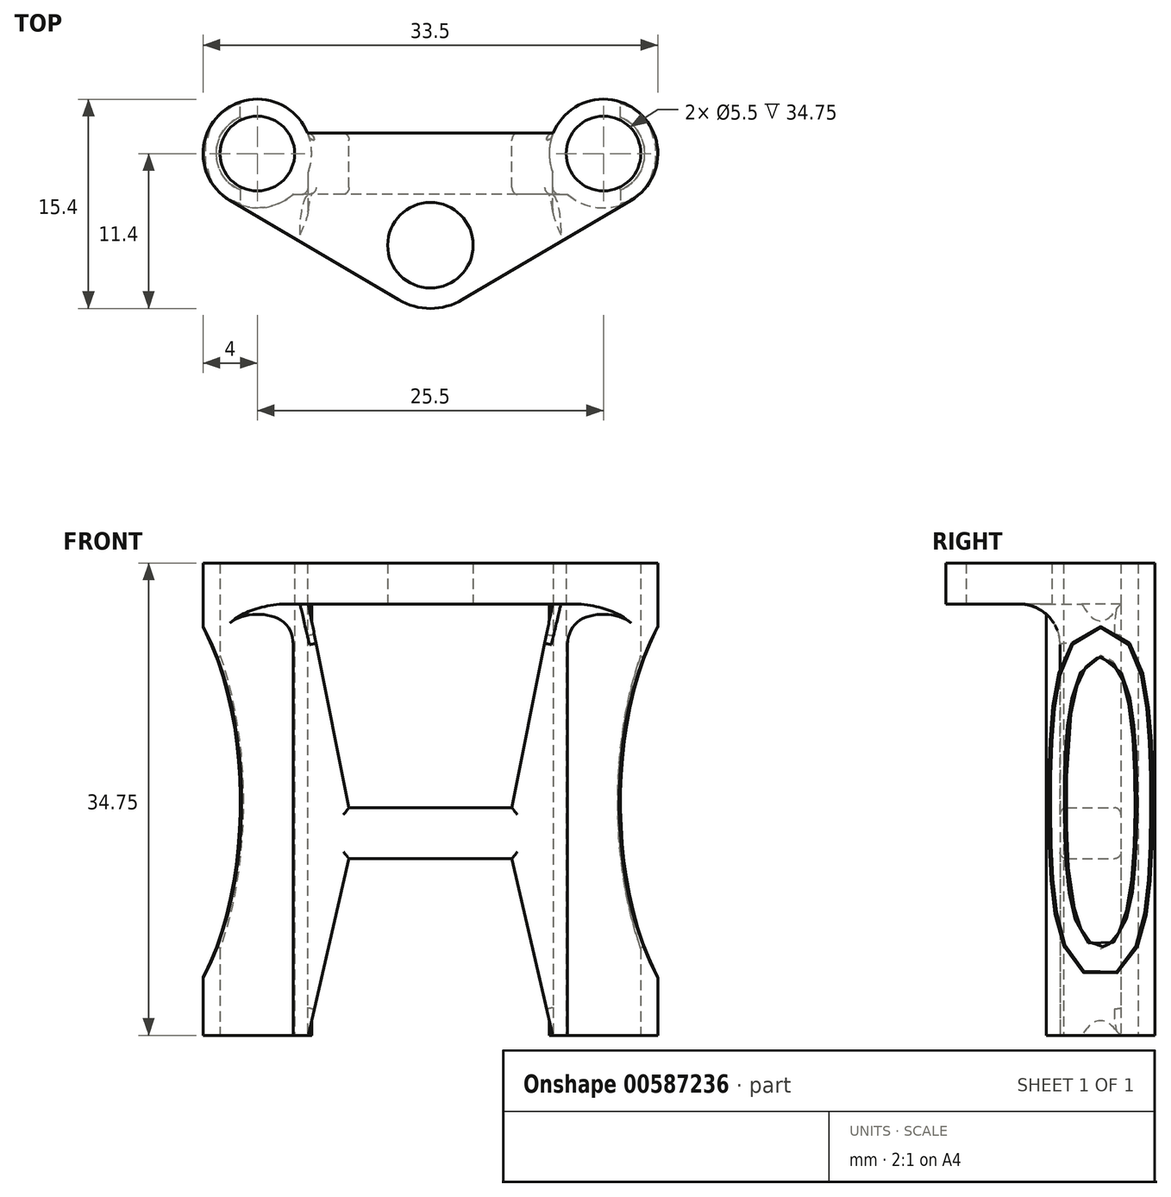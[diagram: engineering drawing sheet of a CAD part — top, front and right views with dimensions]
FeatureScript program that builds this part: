
annotation { "Feature Type Name" : "Feature", "Feature Type Description" : "" }
export const myFeature = defineFeature(function(context is Context, id is Id, definition is map)
    precondition{}
    {
        {
            var Q0;
            Q0=qCreatedBy(makeId("Top.planeOp"),FACE);
            var sketch = newSketch(context, id + "F0", { "sketchPlane" : qUnion([Q0])});
            skCircle(sketch, "E0", {"center": v(0, -6.75) * mm, "radius": 4.65 * mm});
            skCircle(sketch, "E1", {"center": v(0, -6.75) * mm, "radius": 3.15 * mm});
            skCircle(sketch, "E2", {"center": v(-12.75, 0) * mm, "radius": 4 * mm});
            skCircle(sketch, "E3", {"center": v(-12.75, 0) * mm, "radius": 2.75 * mm});
            skCircle(sketch, "E4", {"center": v(12.75, 0) * mm, "radius": 4 * mm});
            skCircle(sketch, "E5", {"center": v(12.75, 0) * mm, "radius": 2.75 * mm});
            skLineSegment(sketch, "E6", {"start": v(0, 0) * mm, "end": v(0, -6.75) * mm});
            skLineSegment(sketch, "E7", {"start": v(-14.78, -3.45) * mm, "end": v(-2.36, -10.76) * mm});
            skLineSegment(sketch, "E8", {"start": v(2.36, -10.76) * mm, "end": v(14.78, -3.45) * mm});
            skLineSegment(sketch, "E9", {"start": v(-9.04, 1.5) * mm, "end": v(9.04, 1.5) * mm});
            skLineSegment(sketch, "E10", {"start": v(-12.75, 0) * mm, "end": v(0, 0) * mm});
            skLineSegment(sketch, "E11", {"start": v(0, 0) * mm, "end": v(12.75, 0) * mm});
            skLineSegment(sketch, "E12", {"start": v(-9.04, -1.5) * mm, "end": v(9.04, -1.5) * mm});
            skSolve(sketch);
        }
        {
            var Q0;
            Q0=makeQuery(id+"F0.imprint","IMPRINT",FACE,{"disambiguationData":[TD([[makeQuery(id+"F0.imprint","IMPRINT",EDGE,{"derivedFrom":sQuery(id+"F0.wireOp",EDGE,"E3")}),-1.0]])]});
            var Q1;
            {var subQ0=sQuery(id+"F0.wireOp",EDGE,"E9");Q1=makeQuery(id+"F0.imprint","IMPRINT",FACE,{"disambiguationData":[TD([[makeQuery(id+"F0.imprint","IMPRINT",EDGE,{"derivedFrom":subQ0}),-1.0]])]});}
            var Q2;
            {var subQ0=sQuery(id+"F0.wireOp",EDGE,"E12");var subQ1=sQuery(id+"F0.wireOp",EDGE,"E2");var subQ2=makeQuery(id+"F0.imprint","INTERSECT",VERTEX,{"derivedFrom":[subQ1,subQ0]});Q2=makeQuery(id+"F0.imprint","IMPRINT",FACE,{"disambiguationData":[TD([[makeQuery(id+"F0.imprint","IMPRINT",EDGE,{"disambiguationData":[TD([[subQ2,-1.0]])],"derivedFrom":subQ1}),-1.0]])]});}
            var Q3;
            Q3=makeQuery(id+"F0.imprint","IMPRINT",FACE,{"disambiguationData":[TD([[makeQuery(id+"F0.imprint","IMPRINT",EDGE,{"derivedFrom":sQuery(id+"F0.wireOp",EDGE,"E5")}),-1.0]])]});
            var Q4;
            {var subQ0=sQuery(id+"F0.wireOp",EDGE,"E12");var subQ1=sQuery(id+"F0.wireOp",EDGE,"E4");var subQ2=makeQuery(id+"F0.imprint","INTERSECT",VERTEX,{"derivedFrom":[subQ1,subQ0]});Q4=makeQuery(id+"F0.imprint","IMPRINT",FACE,{"disambiguationData":[TD([[makeQuery(id+"F0.imprint","IMPRINT",EDGE,{"disambiguationData":[TD([[subQ2,1.0]])],"derivedFrom":subQ1}),-1.0]])]});}
            var Q5;
            {var subQ0=sQuery(id+"F0.wireOp",EDGE,"E7");Q5=makeQuery(id+"F0.imprint","IMPRINT",FACE,{"disambiguationData":[TD([[makeQuery(id+"F0.imprint","IMPRINT",EDGE,{"derivedFrom":subQ0}),1.0]])]});}
            var Q6;
            {var subQ5=sQuery(id+"F0.wireOp",EDGE,"E8");Q6=makeQuery(id+"F0.imprint","IMPRINT",FACE,{"disambiguationData":[TD([[makeQuery(id+"F0.imprint","IMPRINT",EDGE,{"derivedFrom":subQ5}),1.0]])]});}
            var Q7;
            Q7=makeQuery(id+"F0.imprint","IMPRINT",FACE,{"disambiguationData":[TD([[makeQuery(id+"F0.imprint","IMPRINT",EDGE,{"derivedFrom":sQuery(id+"F0.wireOp",EDGE,"E1")}),-1.0]])]});
            extrude(context, id + "F1", {"entities" : qUnion([Q0, Q1, Q2, Q3, Q4, Q5, Q6, Q7]), "depth" : 34.75 * mm, "offsetDistance" : 25 * mm});
        }
        {
            var Q0;
            Q0=qCreatedBy(makeId("Front.planeOp"),FACE);
            var sketch = newSketch(context, id + "F2", { "sketchPlane" : qUnion([Q0])});
            skLineSegment(sketch, "E13", {"start": v(0, 0) * mm, "end": v(-9, 0) * mm});
            skLineSegment(sketch, "E14", {"start": v(-9, 0) * mm, "end": v(-6, 13) * mm});
            skLineSegment(sketch, "E15", {"start": v(-6, 13) * mm, "end": v(6, 13) * mm});
            skLineSegment(sketch, "E16", {"start": v(6, 13) * mm, "end": v(9, 0) * mm});
            skLineSegment(sketch, "E17", {"start": v(9, 0) * mm, "end": v(0, 0) * mm});
            skLineSegment(sketch, "E18", {"start": v(0, 31.75) * mm, "end": v(-9, 31.75) * mm});
            skLineSegment(sketch, "E19", {"start": v(-9, 31.75) * mm, "end": v(-6, 16.75) * mm});
            skLineSegment(sketch, "E20", {"start": v(-6, 16.75) * mm, "end": v(6, 16.75) * mm});
            skLineSegment(sketch, "E21", {"start": v(6, 16.75) * mm, "end": v(9, 31.75) * mm});
            skLineSegment(sketch, "E22", {"start": v(9, 31.75) * mm, "end": v(0, 31.75) * mm});
            skSolve(sketch);
        }
        {
            var Q0;
            Q0 = qSketchRegion(id + "F2", true);
            extrude(context, id + "F3", {"entities" : qUnion([Q0]), "operationType" : NewBodyOperationType.REMOVE, "endBound" : BoundingType.SYMMETRIC, "depth" : 25 * mm, "offsetDistance" : 25 * mm});
        }
        {
            var Q0;
            Q0=qCreatedBy(makeId("Right.planeOp"),FACE);
            var sketch = newSketch(context, id + "F4", { "sketchPlane" : qUnion([Q0])});
            skLineSegment(sketch, "E23", {"start": v(-3, 0) * mm, "end": v(-3, 28.75) * mm});
            skLineSegment(sketch, "E24", {"start": v(-6, 31.75) * mm, "end": v(-18, 31.75) * mm});
            skLineSegment(sketch, "E25", {"start": v(-18, 31.75) * mm, "end": v(-18, 0) * mm});
            skLineSegment(sketch, "E26", {"start": v(-18, 0) * mm, "end": v(-3, 0) * mm});
            skPoint(sketch, "E27.visualSharp", {"position": v(-3, 31.75) * mm});
            skArc(sketch, "E27.filletArc", {"start": v(-3, 28.75) * mm, "mid": v(-3.88, 30.87) * mm, "end": v(-6, 31.75) * mm});
            skSolve(sketch);
        }
        {
            var Q0;
            Q0 = qSketchRegion(id + "F4", true);
            extrude(context, id + "F5", {"entities" : qUnion([Q0]), "operationType" : NewBodyOperationType.REMOVE, "endBound" : BoundingType.SYMMETRIC, "oppositeDirection" : true, "depth" : 35 * mm, "offsetDistance" : 25 * mm});
        }
        {
            var Q0;
            Q0=makeQuery(id+"F5.boolean.opBoolean","INTERSECT",EDGE,{"derivedFrom":[makeQuery(id+"F3.boolean.opBoolean","COPY",FACE,{"derivedFrom":makeQuery(id+"F3.opExtrude","SWEPT_FACE",FACE,{"disambiguationData":[OSD([sQuery(id+"F2.wireOp",EDGE,"E19")])]})}),makeQuery(id+"F5.opExtrude","SWEPT_FACE",FACE,{"disambiguationData":[OSD([sQuery(id+"F4.wireOp",EDGE,"E23")])]})]});
            var Q1;
            Q1=makeQuery(id+"F5.boolean.opBoolean","INTERSECT",EDGE,{"derivedFrom":[makeQuery(id+"F3.boolean.opBoolean","COPY",FACE,{"derivedFrom":makeQuery(id+"F3.opExtrude","SWEPT_FACE",FACE,{"disambiguationData":[OSD([sQuery(id+"F2.wireOp",EDGE,"E20")])]})}),makeQuery(id+"F5.opExtrude","SWEPT_FACE",FACE,{"disambiguationData":[OSD([sQuery(id+"F4.wireOp",EDGE,"E23")])]})]});
            var Q2;
            Q2=makeQuery(id+"F5.boolean.opBoolean","INTERSECT",EDGE,{"derivedFrom":[makeQuery(id+"F3.boolean.opBoolean","COPY",FACE,{"derivedFrom":makeQuery(id+"F3.opExtrude","SWEPT_FACE",FACE,{"disambiguationData":[OSD([sQuery(id+"F2.wireOp",EDGE,"E21")])]})}),makeQuery(id+"F5.opExtrude","SWEPT_FACE",FACE,{"disambiguationData":[OSD([sQuery(id+"F4.wireOp",EDGE,"E23")])]})]});
            var Q3;
            Q3=makeQuery(id+"F5.boolean.opBoolean","INTERSECT",EDGE,{"derivedFrom":[makeQuery(id+"F3.boolean.opBoolean","COPY",FACE,{"derivedFrom":makeQuery(id+"F3.opExtrude","SWEPT_FACE",FACE,{"disambiguationData":[OSD([sQuery(id+"F2.wireOp",EDGE,"E16")])]})}),makeQuery(id+"F5.opExtrude","SWEPT_FACE",FACE,{"disambiguationData":[OSD([sQuery(id+"F4.wireOp",EDGE,"E23")])]})]});
            var Q4;
            Q4=makeQuery(id+"F5.boolean.opBoolean","INTERSECT",EDGE,{"derivedFrom":[makeQuery(id+"F3.boolean.opBoolean","COPY",FACE,{"derivedFrom":makeQuery(id+"F3.opExtrude","SWEPT_FACE",FACE,{"disambiguationData":[OSD([sQuery(id+"F2.wireOp",EDGE,"E15")])]})}),makeQuery(id+"F5.opExtrude","SWEPT_FACE",FACE,{"disambiguationData":[OSD([sQuery(id+"F4.wireOp",EDGE,"E23")])]})]});
            var Q5;
            Q5=makeQuery(id+"F5.boolean.opBoolean","INTERSECT",EDGE,{"derivedFrom":[makeQuery(id+"F3.boolean.opBoolean","COPY",FACE,{"derivedFrom":makeQuery(id+"F3.opExtrude","SWEPT_FACE",FACE,{"disambiguationData":[OSD([sQuery(id+"F2.wireOp",EDGE,"E14")])]})}),makeQuery(id+"F5.opExtrude","SWEPT_FACE",FACE,{"disambiguationData":[OSD([sQuery(id+"F4.wireOp",EDGE,"E23")])]})]});
            var Q6;
            Q6=makeQuery(id+"F3.boolean.opBoolean","INTERSECT",EDGE,{"derivedFrom":[makeQuery(id+"F1.opExtrude","SWEPT_FACE",FACE,{"disambiguationData":[OSD([sQuery(id+"F0.wireOp",EDGE,"E9")])]}),makeQuery(id+"F3.opExtrude","SWEPT_FACE",FACE,{"disambiguationData":[OSD([sQuery(id+"F2.wireOp",EDGE,"E16")])]})]});
            var Q7;
            Q7=makeQuery(id+"F3.boolean.opBoolean","INTERSECT",EDGE,{"derivedFrom":[makeQuery(id+"F1.opExtrude","SWEPT_FACE",FACE,{"disambiguationData":[OSD([sQuery(id+"F0.wireOp",EDGE,"E9")])]}),makeQuery(id+"F3.opExtrude","SWEPT_FACE",FACE,{"disambiguationData":[OSD([sQuery(id+"F2.wireOp",EDGE,"E15")])]})]});
            var Q8;
            Q8=makeQuery(id+"F3.boolean.opBoolean","INTERSECT",EDGE,{"derivedFrom":[makeQuery(id+"F1.opExtrude","SWEPT_FACE",FACE,{"disambiguationData":[OSD([sQuery(id+"F0.wireOp",EDGE,"E9")])]}),makeQuery(id+"F3.opExtrude","SWEPT_FACE",FACE,{"disambiguationData":[OSD([sQuery(id+"F2.wireOp",EDGE,"E14")])]})]});
            var Q9;
            Q9=makeQuery(id+"F3.boolean.opBoolean","INTERSECT",EDGE,{"derivedFrom":[makeQuery(id+"F1.opExtrude","SWEPT_FACE",FACE,{"disambiguationData":[OSD([sQuery(id+"F0.wireOp",EDGE,"E9")])]}),makeQuery(id+"F3.opExtrude","SWEPT_FACE",FACE,{"disambiguationData":[OSD([sQuery(id+"F2.wireOp",EDGE,"E21")])]})]});
            var Q10;
            Q10=makeQuery(id+"F3.boolean.opBoolean","INTERSECT",EDGE,{"derivedFrom":[makeQuery(id+"F1.opExtrude","SWEPT_FACE",FACE,{"disambiguationData":[OSD([sQuery(id+"F0.wireOp",EDGE,"E9")])]}),makeQuery(id+"F3.opExtrude","SWEPT_FACE",FACE,{"disambiguationData":[OSD([sQuery(id+"F2.wireOp",EDGE,"E20")])]})]});
            var Q11;
            Q11=makeQuery(id+"F3.boolean.opBoolean","INTERSECT",EDGE,{"derivedFrom":[makeQuery(id+"F1.opExtrude","SWEPT_FACE",FACE,{"disambiguationData":[OSD([sQuery(id+"F0.wireOp",EDGE,"E9")])]}),makeQuery(id+"F3.opExtrude","SWEPT_FACE",FACE,{"disambiguationData":[OSD([sQuery(id+"F2.wireOp",EDGE,"E19")])]})]});
            fillet(context, id + "F6", {"entities" : qUnion([Q0, Q1, Q2, Q3, Q4, Q5, Q6, Q7, Q8, Q9, Q10, Q11]), "radius" : 0.5 * mm, "tangentPropagation" : true, "allowEdgeOverflow" : false});
        }
        {
            var Q0;
            Q0=qCreatedBy(makeId("Top.planeOp"),FACE);
            var sketch = newSketch(context, id + "F7", { "sketchPlane" : qUnion([Q0])});
            skCircle(sketch, "E28", {"center": v(-12.75, 0) * mm, "radius": 4 * mm});
            skCircle(sketch, "E29", {"center": v(12.75, 0) * mm, "radius": 4 * mm});
            skCircle(sketch, "E30", {"center": v(-12.75, 0) * mm, "radius": 2.75 * mm});
            skCircle(sketch, "E31", {"center": v(12.75, 0) * mm, "radius": 2.75 * mm});
            skSolve(sketch);
        }
        {
            var Q0;
            Q0=makeQuery(id+"F7.imprint","IMPRINT",FACE,{"disambiguationData":[TD([[makeQuery(id+"F7.imprint","IMPRINT",EDGE,{"derivedFrom":sQuery(id+"F7.wireOp",EDGE,"E28")}),1.0]])]});
            var Q1;
            Q1=makeQuery(id+"F7.imprint","IMPRINT",FACE,{"disambiguationData":[TD([[makeQuery(id+"F7.imprint","IMPRINT",EDGE,{"derivedFrom":sQuery(id+"F7.wireOp",EDGE,"E29")}),1.0]])]});
            extrude(context, id + "F8", {"entities" : qUnion([Q0, Q1]), "operationType" : NewBodyOperationType.ADD, "depth" : 34.75 * mm, "offsetDistance" : 25 * mm});
        }
        {
            var Q0;
            Q0=qCreatedBy(makeId("Front.planeOp"),FACE);
            var sketch = newSketch(context, id + "F9", { "sketchPlane" : qUnion([Q0])});
            skEllipse(sketch, "E32", {"center": v(-22.5, 17.16) * mm, "majorRadius": 17.5 * mm, "minorRadius": 8.5 * mm, "majorAxis": v(0, -1)});
            skEllipse(sketch, "E33.MirrorC", {"center": v(22.5, 17.16) * mm, "majorRadius": 17.5 * mm, "minorRadius": 8.5 * mm, "majorAxis": v(0, -1)});
            skSolve(sketch);
        }
        {
            var Q0;
            Q0=makeQuery(id+"F9.imprint","IMPRINT",FACE,{"disambiguationData":[TD([[makeQuery(id+"F9.imprint","IMPRINT",EDGE,{"derivedFrom":sQuery(id+"F9.wireOp",EDGE,"E32")}),1.0]])]});
            var Q1;
            Q1=makeQuery(id+"F9.imprint","IMPRINT",FACE,{"disambiguationData":[TD([[makeQuery(id+"F9.imprint","IMPRINT",EDGE,{"derivedFrom":sQuery(id+"F9.wireOp",EDGE,"E33.MirrorC")}),1.0]])]});
            extrude(context, id + "F10", {"entities" : qUnion([Q0, Q1]), "operationType" : NewBodyOperationType.REMOVE, "endBound" : BoundingType.SYMMETRIC, "oppositeDirection" : true, "depth" : 25 * mm, "offsetDistance" : 25 * mm});
        }
        {
            var Q0;
            Q0=makeQuery(id+"F10.boolean.opBoolean","INTERSECT",EDGE,{"derivedFrom":[makeQuery(id+"F8.boolean.opBoolean","MERGE",FACE,{"derivedFrom":[makeQuery(id+"F1.opExtrude","SWEPT_FACE",FACE,{"disambiguationData":[OSD([sQuery(id+"F0.wireOp",EDGE,"E4")])]}),makeQuery(id+"F8.opExtrude","SWEPT_FACE",FACE,{"disambiguationData":[OSD([sQuery(id+"F7.wireOp",EDGE,"E29")])]})]}),makeQuery(id+"F10.opExtrude","SWEPT_FACE",FACE,{"disambiguationData":[OSD([sQuery(id+"F9.wireOp",EDGE,"E33.MirrorC")])]})]});
            var Q1;
            Q1=makeQuery(id+"F10.boolean.opBoolean","INTERSECT",EDGE,{"derivedFrom":[makeQuery(id+"F8.boolean.opBoolean","MERGE",FACE,{"derivedFrom":[makeQuery(id+"F1.opExtrude","SWEPT_FACE",FACE,{"disambiguationData":[OSD([sQuery(id+"F0.wireOp",EDGE,"E2")])]}),makeQuery(id+"F8.opExtrude","SWEPT_FACE",FACE,{"disambiguationData":[OSD([sQuery(id+"F7.wireOp",EDGE,"E28")])]})]}),makeQuery(id+"F10.opExtrude","SWEPT_FACE",FACE,{"disambiguationData":[OSD([sQuery(id+"F9.wireOp",EDGE,"E32")])]})]});
            var Q2;
            Q2=makeQuery(id+"F10.boolean.opBoolean","INTERSECT",EDGE,{"derivedFrom":[makeQuery(id+"F1.opExtrude","SWEPT_FACE",FACE,{"disambiguationData":[OSD([sQuery(id+"F0.wireOp",EDGE,"E3")])]}),makeQuery(id+"F10.opExtrude","SWEPT_FACE",FACE,{"disambiguationData":[OSD([sQuery(id+"F9.wireOp",EDGE,"E32")])]})]});
            var Q3;
            Q3=makeQuery(id+"F10.boolean.opBoolean","INTERSECT",EDGE,{"derivedFrom":[makeQuery(id+"F1.opExtrude","SWEPT_FACE",FACE,{"disambiguationData":[OSD([sQuery(id+"F0.wireOp",EDGE,"E5")])]}),makeQuery(id+"F10.opExtrude","SWEPT_FACE",FACE,{"disambiguationData":[OSD([sQuery(id+"F9.wireOp",EDGE,"E33.MirrorC")])]})]});
            fillet(context, id + "F11", {"entities" : qUnion([Q0, Q1, Q2, Q3]), "radius" : 0.15 * mm, "tangentPropagation" : true, "allowEdgeOverflow" : false});
        }
    });
